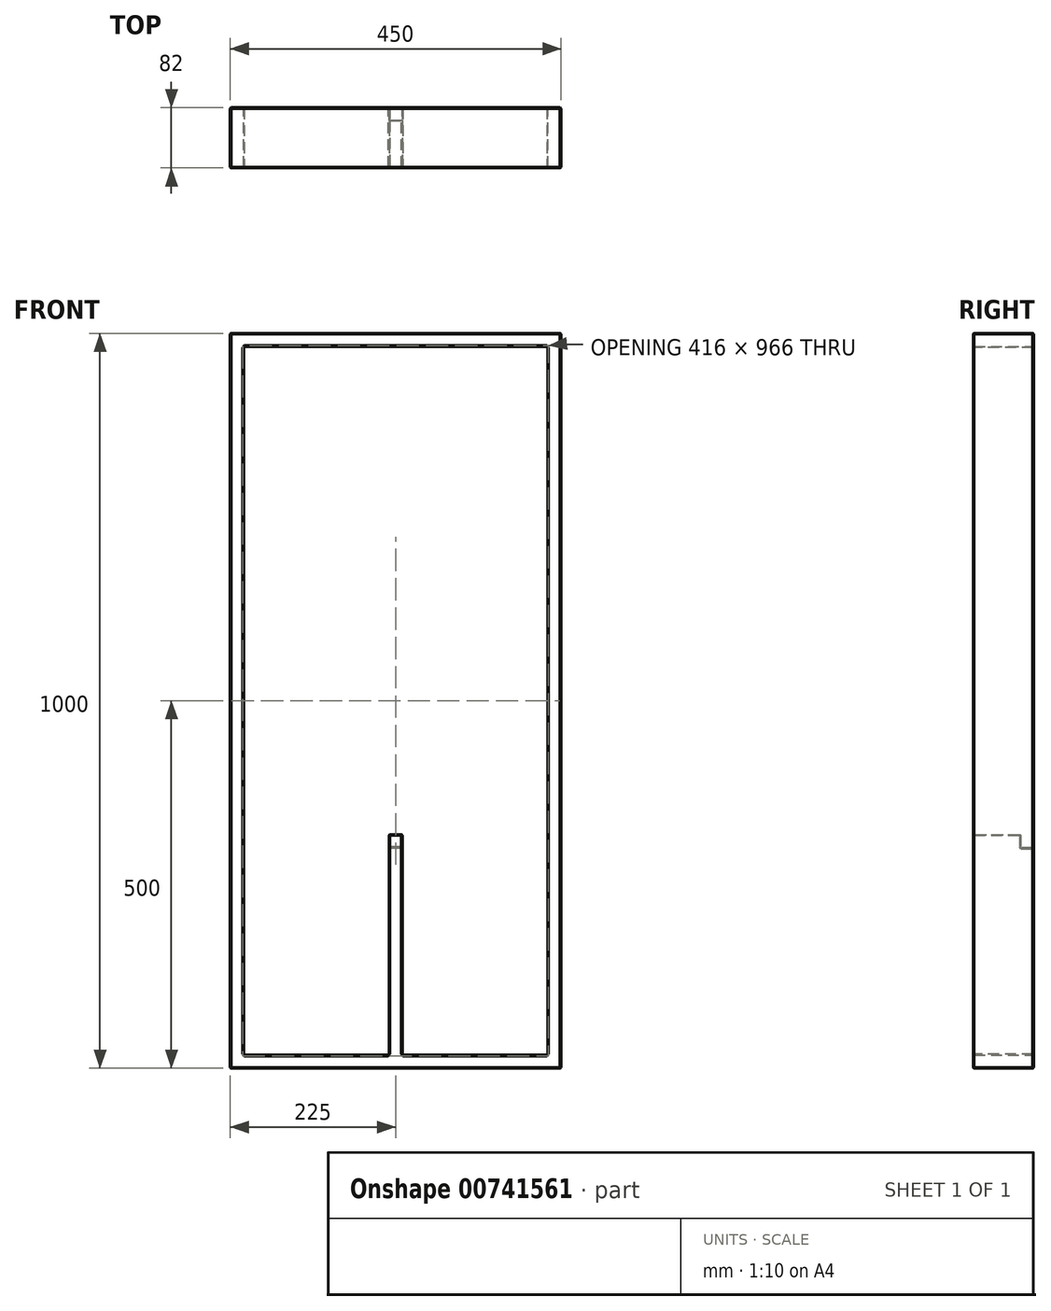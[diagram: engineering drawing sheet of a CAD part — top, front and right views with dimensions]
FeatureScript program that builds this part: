
annotation { "Feature Type Name" : "Feature", "Feature Type Description" : "" }
export const myFeature = defineFeature(function(context is Context, id is Id, definition is map)
    precondition{}
    {
        {
            var Q0;
            Q0=qCreatedBy(makeId("Front.planeOp"),FACE);
            var sketch = newSketch(context, id + "F0", { "sketchPlane" : qUnion([Q0])});
            skLineSegment(sketch, "E0.bottom", {"start": v(-225, 500) * mm, "end": v(225, 500) * mm});
            skLineSegment(sketch, "E0.top", {"start": v(-225, -500) * mm, "end": v(225, -500) * mm});
            skLineSegment(sketch, "E0.left", {"start": v(-225, 500) * mm, "end": v(-225, -500) * mm});
            skLineSegment(sketch, "E0.right", {"start": v(225, 500) * mm, "end": v(225, -500) * mm});
            skLineSegment(sketch, "E1", {"start": v(-225, 500) * mm, "end": v(225, -500) * mm, "construction": true});
            skLineSegment(sketch, "E2.bottom", {"start": v(207, 482) * mm, "end": v(-207, 482) * mm});
            skLineSegment(sketch, "E2.top", {"start": v(207, -482) * mm, "end": v(9, -482) * mm});
            skLineSegment(sketch, "E2.left", {"start": v(207, 482) * mm, "end": v(207, -482) * mm});
            skLineSegment(sketch, "E2.right", {"start": v(-207, 482) * mm, "end": v(-207, -482) * mm});
            skPoint(sketch, "E2.middle", {"position": v(0, 0) * mm});
            skLineSegment(sketch, "E3", {"start": v(-9, -482) * mm, "end": v(-9, -182) * mm});
            skLineSegment(sketch, "E4", {"start": v(-9, -182) * mm, "end": v(9, -182) * mm});
            skLineSegment(sketch, "E5", {"start": v(9, -182) * mm, "end": v(9, -482) * mm});
            skLineSegment(sketch, "E6.trimOffspring", {"start": v(-9, -482) * mm, "end": v(-207, -482) * mm});
            skSolve(sketch);
        }
        {
            var Q0;
            Q0=qSketchRegion(id+"F0",true);
            extrude(context, id + "F1", {"entities" : qUnion([Q0]), "depth" : 82 * mm, "offsetDistance" : 25 * mm});
        }
        {
            var Q0;
            Q0=makeQuery(id+"F1.opExtrude","SWEPT_FACE",FACE,{"disambiguationData":[OSD([sQuery(id+"F0.wireOp",EDGE,"E5")])]});
            var sketch = newSketch(context, id + "F2", { "sketchPlane" : qUnion([Q0])});
            skLineSegment(sketch, "E7.bottom", {"start": v(0, -182) * mm, "end": v(-18, -182) * mm});
            skLineSegment(sketch, "E7.top", {"start": v(0, -200) * mm, "end": v(-18, -200) * mm});
            skLineSegment(sketch, "E7.left", {"start": v(0, -182) * mm, "end": v(0, -200) * mm});
            skLineSegment(sketch, "E7.right", {"start": v(-18, -182) * mm, "end": v(-18, -200) * mm});
            skSolve(sketch);
        }
        {
            var Q0;
            Q0 = qSketchRegion(id + "F2", true);
            extrude(context, id + "F3", {"entities" : qUnion([Q0]), "operationType" : NewBodyOperationType.REMOVE, "oppositeDirection" : true, "depth" : 25 * mm, "offsetDistance" : 25 * mm});
        }
        {
            var Q0;
            Q0=makeQuery(id+"F1.opExtrude","CAP_EDGE",EDGE,{"disambiguationData":[OSD([sQuery(id+"F0.wireOp",EDGE,"E0.bottom")])],"isStart":false});
            var Q1;
            Q1=makeQuery(id+"F1.opExtrude","CAP_EDGE",EDGE,{"disambiguationData":[OSD([sQuery(id+"F0.wireOp",EDGE,"E0.top")])],"isStart":true});
            var Q2;
            Q2=makeQuery(id+"F1.opExtrude","SWEPT_EDGE",EDGE,{"disambiguationData":[OSD([sQuery(id+"F0.wireOp",EDGE,"E0.bottom"),sQuery(id+"F0.wireOp",EDGE,"E0.left")])]});
            var Q3;
            Q3=makeQuery(id+"F1.opExtrude","SWEPT_EDGE",EDGE,{"disambiguationData":[OSD([sQuery(id+"F0.wireOp",EDGE,"E0.bottom"),sQuery(id+"F0.wireOp",EDGE,"E0.right")])]});
            var Q4;
            Q4=makeQuery(id+"F1.opExtrude","SWEPT_EDGE",EDGE,{"disambiguationData":[OSD([sQuery(id+"F0.wireOp",EDGE,"E0.top"),sQuery(id+"F0.wireOp",EDGE,"E0.right")])]});
            var Q5;
            Q5=makeQuery(id+"F1.opExtrude","SWEPT_EDGE",EDGE,{"disambiguationData":[OSD([sQuery(id+"F0.wireOp",EDGE,"E2.top"),sQuery(id+"F0.wireOp",EDGE,"E5")])]});
            var Q6;
            Q6=makeQuery(id+"F1.opExtrude","SWEPT_EDGE",EDGE,{"disambiguationData":[OSD([sQuery(id+"F0.wireOp",EDGE,"E2.right"),sQuery(id+"F0.wireOp",EDGE,"E6.trimOffspring")])]});
            var Q7;
            Q7=makeQuery(id+"F1.opExtrude","CAP_EDGE",EDGE,{"disambiguationData":[OSD([sQuery(id+"F0.wireOp",EDGE,"E0.bottom")])],"isStart":true});
            var Q8;
            Q8=makeQuery(id+"F1.opExtrude","CAP_EDGE",EDGE,{"disambiguationData":[OSD([sQuery(id+"F0.wireOp",EDGE,"E5")])],"isStart":false});
            var Q9;
            Q9=makeQuery(id+"F1.opExtrude","CAP_EDGE",EDGE,{"disambiguationData":[OSD([sQuery(id+"F0.wireOp",EDGE,"E0.right")])],"isStart":true});
            var Q10;
            Q10=makeQuery(id+"F1.opExtrude","CAP_EDGE",EDGE,{"disambiguationData":[OSD([sQuery(id+"F0.wireOp",EDGE,"E6.trimOffspring")])],"isStart":true});
            var Q11;
            Q11=makeQuery(id+"F1.opExtrude","CAP_EDGE",EDGE,{"disambiguationData":[OSD([sQuery(id+"F0.wireOp",EDGE,"E0.right")])],"isStart":false});
            var Q12;
            Q12=makeQuery(id+"F1.opExtrude","CAP_EDGE",EDGE,{"disambiguationData":[OSD([sQuery(id+"F0.wireOp",EDGE,"E2.bottom")])],"isStart":true});
            var Q13;
            Q13=makeQuery(id+"F1.opExtrude","CAP_EDGE",EDGE,{"disambiguationData":[OSD([sQuery(id+"F0.wireOp",EDGE,"E2.top")])],"isStart":true});
            var Q14;
            Q14=makeQuery(id+"F1.opExtrude","CAP_EDGE",EDGE,{"disambiguationData":[OSD([sQuery(id+"F0.wireOp",EDGE,"E2.left")])],"isStart":true});
            var Q15;
            Q15=makeQuery(id+"F3.boolean.opBoolean","COPY",EDGE,{"derivedFrom":makeQuery(id+"F3.opExtrude","CAP_EDGE",EDGE,{"disambiguationData":[OSD([sQuery(id+"F2.wireOp",EDGE,"E7.top")])],"isStart":true})});
            var Q16;
            Q16=makeQuery(id+"F1.opExtrude","CAP_EDGE",EDGE,{"disambiguationData":[OSD([sQuery(id+"F0.wireOp",EDGE,"E0.top")])],"isStart":false});
            var Q17;
            Q17=makeQuery(id+"F1.opExtrude","SWEPT_EDGE",EDGE,{"disambiguationData":[OSD([sQuery(id+"F0.wireOp",EDGE,"E0.top"),sQuery(id+"F0.wireOp",EDGE,"E0.left")])]});
            var Q18;
            Q18=makeQuery(id+"F1.opExtrude","SWEPT_EDGE",EDGE,{"disambiguationData":[OSD([sQuery(id+"F0.wireOp",EDGE,"E2.bottom"),sQuery(id+"F0.wireOp",EDGE,"E2.left")])]});
            var Q19;
            Q19=makeQuery(id+"F1.opExtrude","SWEPT_EDGE",EDGE,{"disambiguationData":[OSD([sQuery(id+"F0.wireOp",EDGE,"E2.bottom"),sQuery(id+"F0.wireOp",EDGE,"E2.right")])]});
            var Q20;
            Q20=makeQuery(id+"F1.opExtrude","SWEPT_EDGE",EDGE,{"disambiguationData":[OSD([sQuery(id+"F0.wireOp",EDGE,"E2.top"),sQuery(id+"F0.wireOp",EDGE,"E2.left")])]});
            var Q21;
            Q21=makeQuery(id+"F1.opExtrude","SWEPT_EDGE",EDGE,{"disambiguationData":[OSD([sQuery(id+"F0.wireOp",EDGE,"E3"),sQuery(id+"F0.wireOp",EDGE,"E6.trimOffspring")])]});
            var Q22;
            Q22=makeQuery(id+"F3.boolean.opBoolean","COPY",EDGE,{"derivedFrom":makeQuery(id+"F3.opExtrude","SWEPT_EDGE",EDGE,{"disambiguationData":[OSD([sQuery(id+"F0.wireOp",EDGE,"E5"),sQuery(id+"F2.wireOp",EDGE,"E7.top"),sQuery(id+"F2.wireOp",EDGE,"E7.left")])]})});
            var Q23;
            Q23=makeQuery(id+"F3.boolean.opBoolean","COPY",EDGE,{"derivedFrom":makeQuery(id+"F3.opExtrude","SWEPT_EDGE",EDGE,{"disambiguationData":[OSD([sQuery(id+"F0.wireOp",EDGE,"E4"),sQuery(id+"F0.wireOp",EDGE,"E5"),sQuery(id+"F2.wireOp",EDGE,"E7.bottom"),sQuery(id+"F2.wireOp",EDGE,"E7.right")])]})});
            var Q24;
            Q24=makeQuery(id+"F1.opExtrude","CAP_EDGE",EDGE,{"disambiguationData":[OSD([sQuery(id+"F0.wireOp",EDGE,"E3")])],"isStart":false});
            var Q25;
            Q25=makeQuery(id+"F1.opExtrude","CAP_EDGE",EDGE,{"disambiguationData":[OSD([sQuery(id+"F0.wireOp",EDGE,"E4")])],"isStart":false});
            var Q26;
            Q26=makeQuery(id+"F1.opExtrude","CAP_EDGE",EDGE,{"disambiguationData":[OSD([sQuery(id+"F0.wireOp",EDGE,"E0.left")])],"isStart":true});
            var Q27;
            Q27=makeQuery(id+"F1.opExtrude","CAP_EDGE",EDGE,{"disambiguationData":[OSD([sQuery(id+"F0.wireOp",EDGE,"E0.left")])],"isStart":false});
            var Q28;
            Q28=makeQuery(id+"F1.opExtrude","CAP_EDGE",EDGE,{"disambiguationData":[OSD([sQuery(id+"F0.wireOp",EDGE,"E6.trimOffspring")])],"isStart":false});
            var Q29;
            Q29=makeQuery(id+"F3.boolean.opBoolean","COPY",EDGE,{"derivedFrom":makeQuery(id+"F3.opExtrude","SWEPT_EDGE",EDGE,{"disambiguationData":[OSD([sQuery(id+"F2.wireOp",EDGE,"E7.top"),sQuery(id+"F2.wireOp",EDGE,"E7.right")])]})});
            var Q30;
            Q30=makeQuery(id+"F1.opExtrude","CAP_EDGE",EDGE,{"disambiguationData":[OSD([sQuery(id+"F0.wireOp",EDGE,"E2.bottom")])],"isStart":false});
            var Q31;
            Q31=makeQuery(id+"F1.opExtrude","CAP_EDGE",EDGE,{"disambiguationData":[OSD([sQuery(id+"F0.wireOp",EDGE,"E2.top")])],"isStart":false});
            var Q32;
            Q32=makeQuery(id+"F1.opExtrude","CAP_EDGE",EDGE,{"disambiguationData":[OSD([sQuery(id+"F0.wireOp",EDGE,"E2.left")])],"isStart":false});
            var Q33;
            Q33=makeQuery(id+"F1.opExtrude","CAP_EDGE",EDGE,{"disambiguationData":[OSD([sQuery(id+"F0.wireOp",EDGE,"E2.right")])],"isStart":true});
            var Q34;
            Q34=makeQuery(id+"F1.opExtrude","CAP_EDGE",EDGE,{"disambiguationData":[OSD([sQuery(id+"F0.wireOp",EDGE,"E2.right")])],"isStart":false});
            var Q35;
            Q35=makeQuery(id+"F3.boolean.opBoolean","COPY",EDGE,{"derivedFrom":makeQuery(id+"F3.opExtrude","CAP_EDGE",EDGE,{"disambiguationData":[OSD([sQuery(id+"F2.wireOp",EDGE,"E7.right")])],"isStart":true})});
            var Q36;
            Q36=makeQuery(id+"F3.boolean.opBoolean","INTERSECT",EDGE,{"derivedFrom":[makeQuery(id+"F1.opExtrude","SWEPT_FACE",FACE,{"disambiguationData":[OSD([sQuery(id+"F0.wireOp",EDGE,"E3")])]}),makeQuery(id+"F3.opExtrude","SWEPT_FACE",FACE,{"disambiguationData":[OSD([sQuery(id+"F2.wireOp",EDGE,"E7.top")])]})]});
            var Q37;
            Q37=makeQuery(id+"F3.boolean.opBoolean","INTERSECT",EDGE,{"derivedFrom":[makeQuery(id+"F1.opExtrude","SWEPT_FACE",FACE,{"disambiguationData":[OSD([sQuery(id+"F0.wireOp",EDGE,"E3")])]}),makeQuery(id+"F3.opExtrude","SWEPT_FACE",FACE,{"disambiguationData":[OSD([sQuery(id+"F2.wireOp",EDGE,"E7.right")])]})]});
            var Q38;
            Q38=makeQuery(id+"F1.opExtrude","CAP_EDGE",EDGE,{"disambiguationData":[OSD([sQuery(id+"F0.wireOp",EDGE,"E3")])],"isStart":true});
            var Q39;
            Q39=makeQuery(id+"F1.opExtrude","CAP_EDGE",EDGE,{"disambiguationData":[OSD([sQuery(id+"F0.wireOp",EDGE,"E5")])],"isStart":true});
            var Q40;
            Q40=makeQuery(id+"F1.opExtrude","SWEPT_EDGE",EDGE,{"disambiguationData":[OSD([sQuery(id+"F0.wireOp",EDGE,"E4"),sQuery(id+"F0.wireOp",EDGE,"E5")])]});
            var Q41;
            Q41=makeQuery(id+"F1.opExtrude","SWEPT_EDGE",EDGE,{"disambiguationData":[OSD([sQuery(id+"F0.wireOp",EDGE,"E3"),sQuery(id+"F0.wireOp",EDGE,"E4")])]});
            chamfer(context, id + "F4", {"entities" : qUnion([Q0, Q1, Q2, Q3, Q4, Q5, Q6, Q7, Q8, Q9, Q10, Q11, Q12, Q13, Q14, Q15, Q16, Q17, Q18, Q19, Q20, Q21, Q22, Q23, Q24, Q25, Q26, Q27, Q28, Q29, Q30, Q31, Q32, Q33, Q34, Q35, Q36, Q37, Q38, Q39, Q40, Q41]), "width" : 1 * mm, "tangentPropagation" : true});
        }
    });
